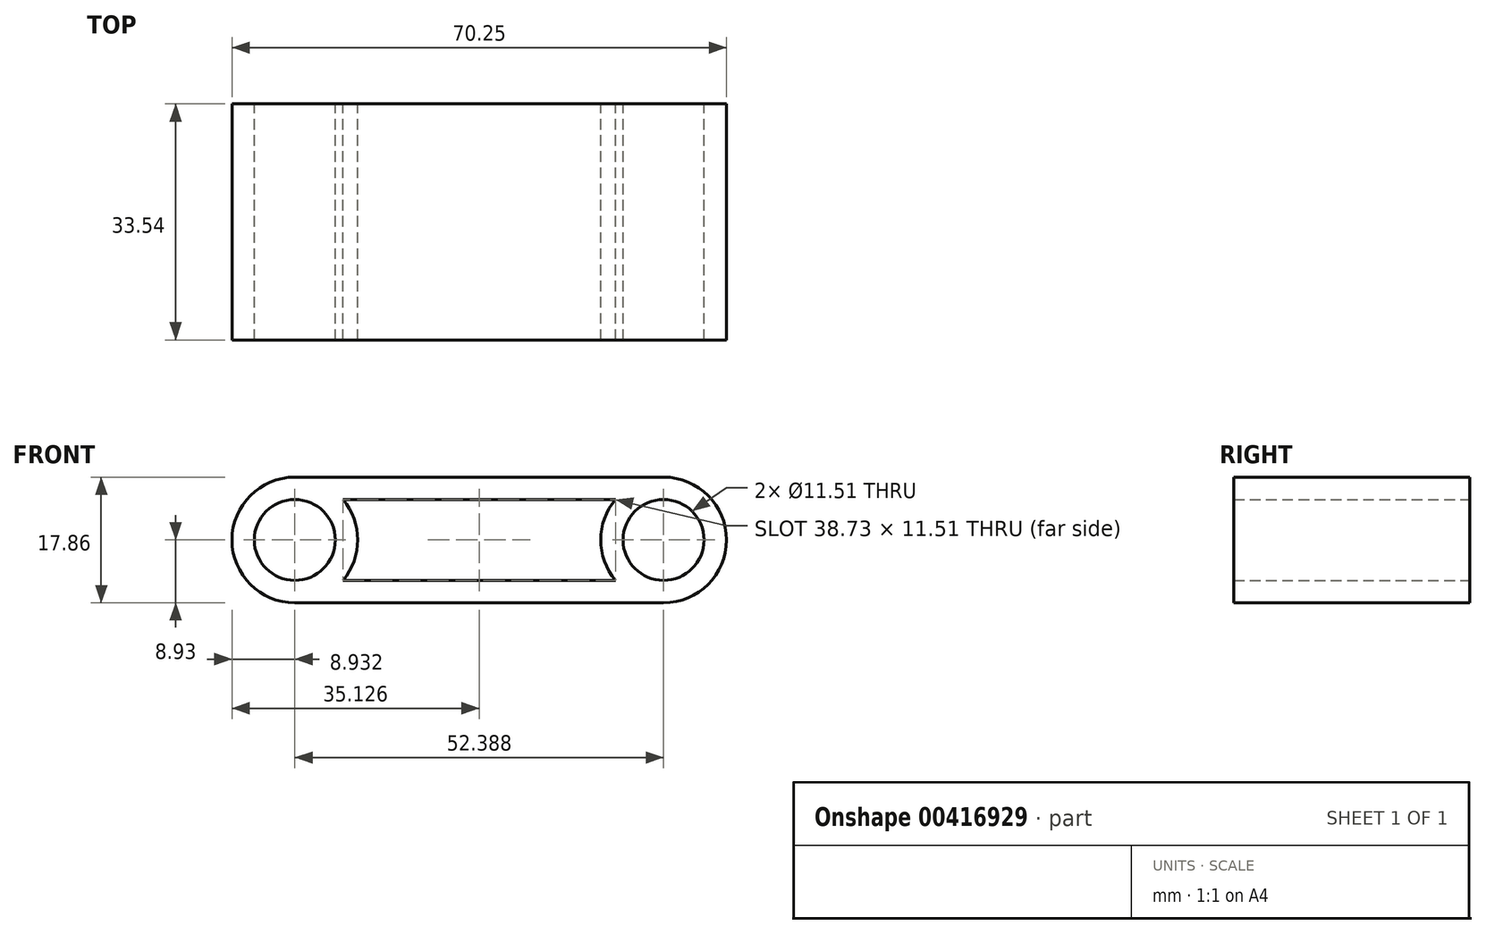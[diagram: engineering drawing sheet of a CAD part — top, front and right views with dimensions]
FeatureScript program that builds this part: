
annotation { "Feature Type Name" : "Feature", "Feature Type Description" : "" }
export const myFeature = defineFeature(function(context is Context, id is Id, definition is map)
    precondition{}
    {
        {
            var Q0;
            Q0=qCreatedBy(makeId("Front.planeOp"),FACE);
            var sketch = newSketch(context, id + "F0", { "sketchPlane" : qUnion([Q0])});
            skCircle(sketch, "E0", {"center": v(0, 0) * mm, "radius": 5.75 * mm});
            skArc(sketch, "E1", {"start": v(-6.83, 5.75) * mm, "mid": v(-8.93, 0) * mm, "end": v(-6.83, -5.75) * mm});
            skLineSegment(sketch, "E2", {"start": v(0, 0) * mm, "end": v(-52.39, 0) * mm, "construction": true});
            skCircle(sketch, "E3", {"center": v(-52.39, 0) * mm, "radius": 5.75 * mm});
            skArc(sketch, "E4", {"start": v(-45.56, -5.75) * mm, "mid": v(-43.46, 0) * mm, "end": v(-45.56, 5.75) * mm});
            skLineSegment(sketch, "E5", {"start": v(-52.39, 8.93) * mm, "end": v(0, 8.93) * mm});
            skLineSegment(sketch, "E6", {"start": v(-45.56, 5.75) * mm, "end": v(-6.83, 5.75) * mm});
            skLineSegment(sketch, "E7", {"start": v(-45.56, -5.75) * mm, "end": v(-6.83, -5.75) * mm});
            skLineSegment(sketch, "E8", {"start": v(-52.39, -8.93) * mm, "end": v(0, -8.93) * mm});
            skLineSegment(sketch, "E9", {"start": v(-26.2, -8.93) * mm, "end": v(-26.2, -5.75) * mm, "construction": true});
            skLineSegment(sketch, "E10", {"start": v(-26.2, 8.93) * mm, "end": v(-26.2, 5.75) * mm, "construction": true});
            skArc(sketch, "E11.trimOffspring", {"start": v(0, -8.93) * mm, "mid": v(8.93, 0) * mm, "end": v(0, 8.93) * mm});
            skArc(sketch, "E12.trimOffspring", {"start": v(-52.39, 8.93) * mm, "mid": v(-61.32, 0) * mm, "end": v(-52.39, -8.93) * mm});
            skSolve(sketch);
        }
        {
            var Q0;
            Q0=makeQuery(id+"F0.imprint","IMPRINT",FACE,{"disambiguationData":[TD([[makeQuery(id+"F0.imprint","IMPRINT",EDGE,{"derivedFrom":sQuery(id+"F0.wireOp",EDGE,"E0")}),-1.0]])]});
            extrude(context, id + "F1", {"entities" : qUnion([Q0]), "depth" : 33.54 * mm});
        }
    });
